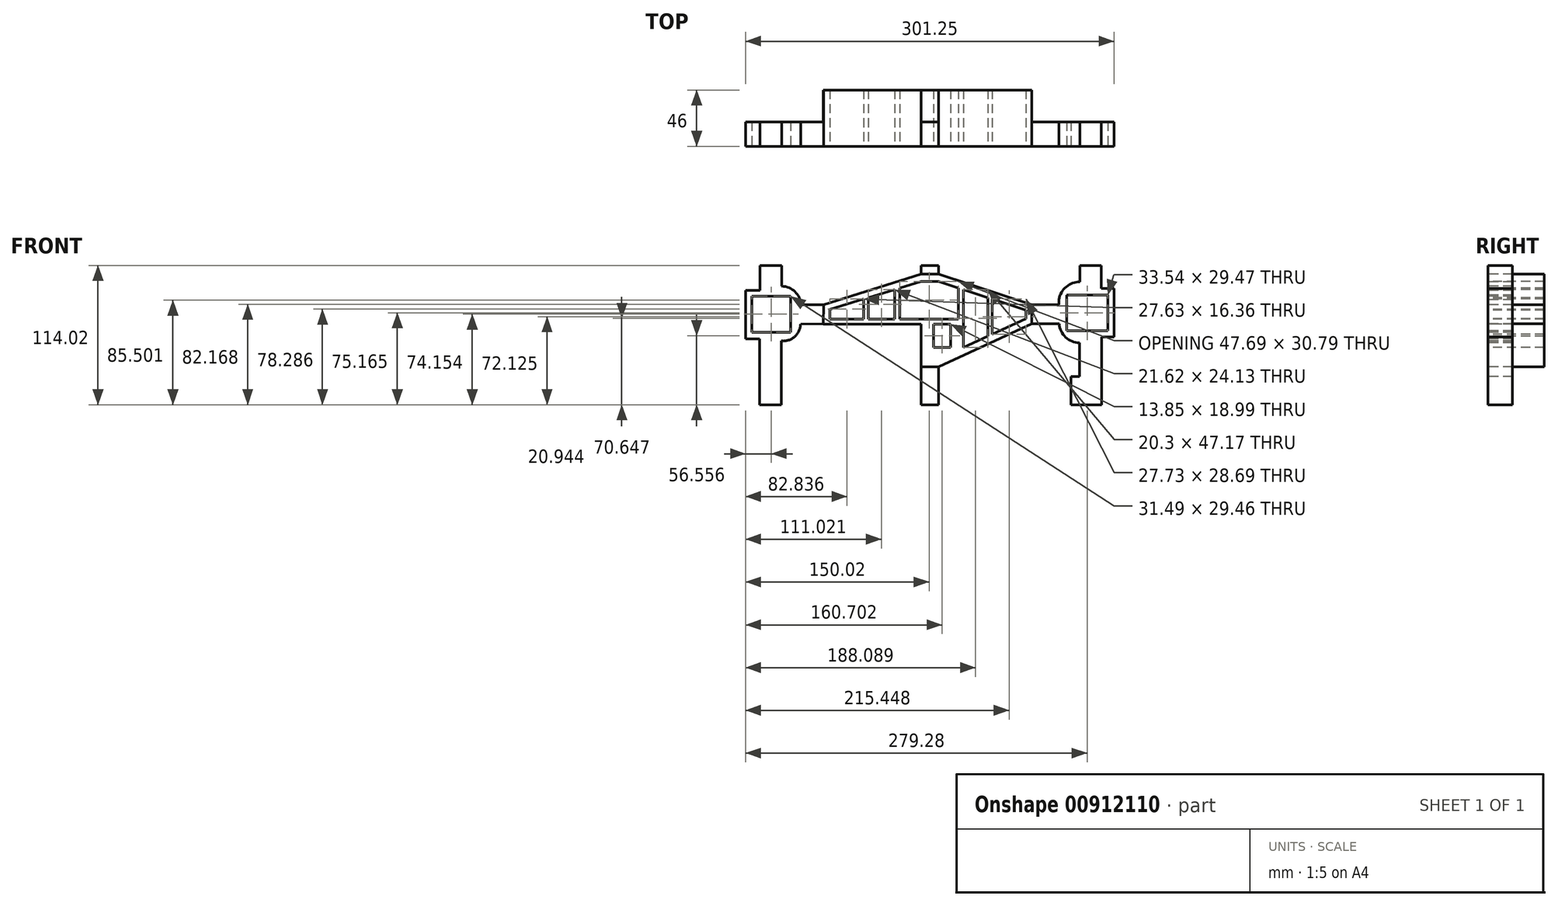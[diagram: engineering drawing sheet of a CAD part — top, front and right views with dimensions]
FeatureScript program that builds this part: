
annotation { "Feature Type Name" : "Feature", "Feature Type Description" : "" }
export const myFeature = defineFeature(function(context is Context, id is Id, definition is map)
    precondition{}
    {
        {
            var Q0;
            Q0=qCreatedBy(makeId("Front.planeOp"),FACE);
            var sketch = newSketch(context, id + "F0", { "sketchPlane" : qUnion([Q0])});
            skPoint(sketch, "E0.centerSnap0", {"position": v(-16.6, 78.73) * mm});
            skPoint(sketch, "E1.end.orphan", {"position": v(95.9, 7.77) * mm});
            skPoint(sketch, "E2.trimOffspring.end.orphan", {"position": v(-16.6, -51.27) * mm});
            skPoint(sketch, "E3.trimOffspring.end.orphan", {"position": v(97, 81.09) * mm});
            skPoint(sketch, "E4.endSnap0", {"position": v(95.9, 12.77) * mm});
            skPoint(sketch, "E5.trimOffspring.end.orphan", {"position": v(95.9, 11.34) * mm});
            skLineSegment(sketch, "E6.trimOffspring", {"start": v(-141.6, 27.34) * mm, "end": v(-141.6, 27.21) * mm});
            skLineSegment(sketch, "E7", {"start": v(-155.63, 47.28) * mm, "end": v(-155.63, 67.63) * mm});
            skLineSegment(sketch, "E8", {"start": v(-137.79, 50.54) * mm, "end": v(-137.79, 67.63) * mm});
            skArc(sketch, "E9", {"start": v(-122.48, 35.44) * mm, "mid": v(-127.04, 46.13) * mm, "end": v(-137.79, 50.54) * mm});
            skLineSegment(sketch, "E10", {"start": v(-155.63, 47.28) * mm, "end": v(-167.43, 47.28) * mm});
            skLineSegment(sketch, "E11", {"start": v(-155.87, 7.65) * mm, "end": v(-167.43, 7.65) * mm});
            skArc(sketch, "E12", {"start": v(88.97, 19.87) * mm, "mid": v(94.32, 8.84) * mm, "end": v(105.67, 4.2) * mm});
            skArc(sketch, "E13", {"start": v(106.05, 54.28) * mm, "mid": v(94.73, 50.14) * mm, "end": v(88.74, 39.68) * mm});
            skLineSegment(sketch, "E14", {"start": v(123.75, 9.23) * mm, "end": v(133.82, 9.23) * mm});
            skLineSegment(sketch, "E15", {"start": v(123.42, 67.63) * mm, "end": v(123.42, 48.8) * mm});
            skLineSegment(sketch, "E16", {"start": v(106.05, 54.28) * mm, "end": v(106.05, 67.63) * mm});
            skLineSegment(sketch, "E17", {"start": v(105.67, 4.2) * mm, "end": v(105.67, -23.42) * mm});
            skLineSegment(sketch, "E18", {"start": v(123.75, 9.23) * mm, "end": v(123.75, -42.87) * mm});
            skLineSegment(sketch, "E19", {"start": v(-122.48, 35.44) * mm, "end": v(-103.75, 35.44) * mm});
            skLineSegment(sketch, "E20", {"start": v(-122.48, 19.66) * mm, "end": v(-103.97, 19.73) * mm});
            skLineSegment(sketch, "E21", {"start": v(-103.75, 35.44) * mm, "end": v(-23.98, 60.68) * mm});
            skLineSegment(sketch, "E22", {"start": v(-23.98, -15.49) * mm, "end": v(-23.98, -46.39) * mm});
            skLineSegment(sketch, "E23", {"start": v(-9.79, -15.49) * mm, "end": v(-9.79, -46.39) * mm});
            skLineSegment(sketch, "E24", {"start": v(-23.98, 60.68) * mm, "end": v(-23.98, 67.63) * mm});
            skLineSegment(sketch, "E25", {"start": v(-9.79, 60.57) * mm, "end": v(-9.79, 67.63) * mm});
            skLineSegment(sketch, "E26", {"start": v(-103.97, 19.73) * mm, "end": v(-103.8, 19.66) * mm});
            skLineSegment(sketch, "E27", {"start": v(-9.79, -15.49) * mm, "end": v(66.68, 19.87) * mm});
            skLineSegment(sketch, "E28", {"start": v(-23.98, 54.5) * mm, "end": v(-9.79, 54.5) * mm});
            skLineSegment(sketch, "E29", {"start": v(88.74, 35.45) * mm, "end": v(88.74, 39.68) * mm});
            skLineSegment(sketch, "E30.trimOffspring", {"start": v(66.68, 35.45) * mm, "end": v(88.74, 35.45) * mm});
            skPoint(sketch, "E31.end.orphan", {"position": v(-103.75, 29.5) * mm});
            skPoint(sketch, "E32.orphan", {"position": v(-103.75, 25.95) * mm});
            skLineSegment(sketch, "E33", {"start": v(-98.4, 23.71) * mm, "end": v(-98.4, 31.56) * mm});
            skLineSegment(sketch, "E34", {"start": v(-98.4, 31.56) * mm, "end": v(-70.78, 40.08) * mm});
            skLineSegment(sketch, "E35", {"start": v(-9.79, 60.57) * mm, "end": v(66.68, 35.45) * mm});
            skLineSegment(sketch, "E36", {"start": v(-9.79, 54.5) * mm, "end": v(6.43, 49.18) * mm});
            skLineSegment(sketch, "E37", {"start": v(61.88, 30.97) * mm, "end": v(61.88, 23.97) * mm});
            skLineSegment(sketch, "E38", {"start": v(61.88, 23.97) * mm, "end": v(34.15, 11.4) * mm});
            skLineSegment(sketch, "E39.trimOffspring", {"start": v(66.68, 19.87) * mm, "end": v(88.97, 19.87) * mm});
            skLineSegment(sketch, "E40", {"start": v(98.61, -25.17) * mm, "end": v(98.61, -46.39) * mm});
            skLineSegment(sketch, "E41", {"start": v(-70.78, 40.08) * mm, "end": v(-70.78, 23.71) * mm});
            skLineSegment(sketch, "E42", {"start": v(-67.22, 41.18) * mm, "end": v(-67.22, 23.71) * mm});
            skLineSegment(sketch, "E43.trimOffspring", {"start": v(-67.22, 41.18) * mm, "end": v(-45.6, 47.84) * mm});
            skLineSegment(sketch, "E44.trimOffspring", {"start": v(-89.2, 19.66) * mm, "end": v(-89.63, 19.85) * mm});
            skLineSegment(sketch, "E45", {"start": v(98.61, -25.17) * mm, "end": v(98.61, -23.42) * mm});
            skLineSegment(sketch, "E46", {"start": v(98.61, -23.42) * mm, "end": v(105.67, -23.42) * mm});
            skLineSegment(sketch, "E47", {"start": v(34.15, 40.08) * mm, "end": v(34.15, 11.4) * mm});
            skLineSegment(sketch, "E48", {"start": v(30.8, 41.18) * mm, "end": v(30.8, 9.88) * mm});
            skLineSegment(sketch, "E49.trimOffspring", {"start": v(34.15, 40.08) * mm, "end": v(61.88, 30.97) * mm});
            skLineSegment(sketch, "E50.trimOffspring", {"start": v(30.8, 9.88) * mm, "end": v(10.51, 0.67) * mm});
            skLineSegment(sketch, "E51", {"start": v(-45.6, 47.84) * mm, "end": v(-45.6, 23.71) * mm});
            skLineSegment(sketch, "E52", {"start": v(-41.26, 49.18) * mm, "end": v(-41.26, 23.71) * mm});
            skLineSegment(sketch, "E53", {"start": v(6.43, 49.18) * mm, "end": v(6.43, 23.71) * mm});
            skLineSegment(sketch, "E54", {"start": v(10.51, 47.84) * mm, "end": v(10.51, 0.67) * mm});
            skLineSegment(sketch, "E55.trimOffspring", {"start": v(-41.26, 49.18) * mm, "end": v(-23.98, 54.5) * mm});
            skLineSegment(sketch, "E56.trimOffspring", {"start": v(10.51, 47.84) * mm, "end": v(30.8, 41.18) * mm});
            skLineSegment(sketch, "E57.trimOffspring", {"start": v(-103.8, 35.44) * mm, "end": v(-103.8, 19.66) * mm});
            skLineSegment(sketch, "E58.trimOffspring", {"start": v(66.68, 19.87) * mm, "end": v(66.68, 35.45) * mm});
            skLineSegment(sketch, "E59", {"start": v(-103.8, 19.66) * mm, "end": v(-23.98, 19.66) * mm});
            skLineSegment(sketch, "E60", {"start": v(-23.98, 19.66) * mm, "end": v(-23.98, -15.49) * mm});
            skLineSegment(sketch, "E61", {"start": v(-98.4, 23.71) * mm, "end": v(-70.78, 23.71) * mm});
            skLineSegment(sketch, "E62.bottom", {"start": v(-13.65, 19.66) * mm, "end": v(0.2, 19.66) * mm});
            skLineSegment(sketch, "E62.top", {"start": v(-13.65, 0.67) * mm, "end": v(0.2, 0.67) * mm});
            skLineSegment(sketch, "E62.left", {"start": v(-13.65, 19.66) * mm, "end": v(-13.65, 0.67) * mm});
            skLineSegment(sketch, "E62.right", {"start": v(0.2, 19.66) * mm, "end": v(0.2, 0.67) * mm});
            skLineSegment(sketch, "E63.trimOffspring", {"start": v(-67.22, 23.71) * mm, "end": v(-45.6, 23.71) * mm});
            skLineSegment(sketch, "E64.trimOffspring", {"start": v(-41.26, 23.71) * mm, "end": v(6.43, 23.71) * mm});
            skLineSegment(sketch, "E65", {"start": v(-23.98, 60.68) * mm, "end": v(-9.79, 60.57) * mm});
            skPoint(sketch, "E66.start.orphan", {"position": v(-103.75, 77.48) * mm});
            skPoint(sketch, "E67.start.orphan", {"position": v(66.68, -52.27) * mm});
            skLineSegment(sketch, "E68", {"start": v(-23.98, -15.49) * mm, "end": v(-9.79, -15.49) * mm});
            skLineSegment(sketch, "E69", {"start": v(123.42, 48.8) * mm, "end": v(133.82, 48.8) * mm});
            skLineSegment(sketch, "E70", {"start": v(-155.63, 67.63) * mm, "end": v(-137.79, 67.63) * mm});
            skLineSegment(sketch, "E71", {"start": v(-167.43, 47.28) * mm, "end": v(-167.43, 7.65) * mm});
            skLineSegment(sketch, "E72", {"start": v(-138.17, -46.38) * mm, "end": v(-155.87, -46.36) * mm});
            skLineSegment(sketch, "E73", {"start": v(-138.17, 5.8) * mm, "end": v(-138.17, -46.38) * mm});
            skLineSegment(sketch, "E74", {"start": v(-155.87, 7.65) * mm, "end": v(-155.87, -46.36) * mm});
            skLineSegment(sketch, "E75", {"start": v(-23.98, -46.39) * mm, "end": v(-9.79, -46.39) * mm});
            skLineSegment(sketch, "E76", {"start": v(98.61, -46.39) * mm, "end": v(123.75, -46.39) * mm});
            skPoint(sketch, "E77.orphan", {"position": v(-167.43, -46.35) * mm});
            skPoint(sketch, "E78.start.orphan", {"position": v(-174.59, -41.81) * mm});
            skPoint(sketch, "E79.start.orphan", {"position": v(-164.6, -52.27) * mm});
            skLineSegment(sketch, "E80", {"start": v(106.05, 67.63) * mm, "end": v(123.42, 67.63) * mm});
            skLineSegment(sketch, "E81", {"start": v(133.82, 48.8) * mm, "end": v(133.82, 9.23) * mm});
            skLineSegment(sketch, "E82", {"start": v(123.75, -42.87) * mm, "end": v(123.75, -46.39) * mm});
            skPoint(sketch, "E83.center.orphan", {"position": v(132.35, -42.27) * mm});
            skPoint(sketch, "E83.end.orphan", {"position": v(142.34, -42.53) * mm});
            skPoint(sketch, "E84.orphan", {"position": v(133.82, -46.39) * mm});
            skPoint(sketch, "E85.end.orphan", {"position": v(132.35, 77.22) * mm});
            skPoint(sketch, "E85.start.orphan", {"position": v(142.34, 68.42) * mm});
            skLineSegment(sketch, "E86", {"start": v(-23.98, 67.63) * mm, "end": v(-9.79, 67.63) * mm});
            skPoint(sketch, "E87.orphan", {"position": v(-122.48, -46.4) * mm});
            skPoint(sketch, "E88.start.orphan", {"position": v(-158.57, 67.63) * mm});
            skPoint(sketch, "E89.center.orphan", {"position": v(-164.6, 67.54) * mm});
            skPoint(sketch, "E89.end.orphan", {"position": v(-174.59, 67.83) * mm});
            skPoint(sketch, "E90", {"position": v(-45.6, 53.83) * mm});
            skPoint(sketch, "E91", {"position": v(10.51, 53.9) * mm});
            skPoint(sketch, "E92.firstSnap0", {"position": v(128.62, 48.8) * mm});
            skLineSegment(sketch, "E92.bottom", {"start": v(128.62, 43.51) * mm, "end": v(95.08, 43.51) * mm});
            skLineSegment(sketch, "E92.top", {"start": v(128.62, 14.04) * mm, "end": v(95.08, 14.04) * mm});
            skLineSegment(sketch, "E92.left", {"start": v(128.62, 43.51) * mm, "end": v(128.62, 14.04) * mm});
            skLineSegment(sketch, "E92.right", {"start": v(95.08, 43.51) * mm, "end": v(95.08, 14.04) * mm});
            skLineSegment(sketch, "E93.bottom", {"start": v(-130.74, 42.5) * mm, "end": v(-162.23, 42.5) * mm});
            skLineSegment(sketch, "E93.top", {"start": v(-130.74, 13.03) * mm, "end": v(-162.23, 13.03) * mm});
            skLineSegment(sketch, "E93.left", {"start": v(-130.74, 42.5) * mm, "end": v(-130.74, 13.03) * mm});
            skLineSegment(sketch, "E93.right", {"start": v(-162.23, 42.5) * mm, "end": v(-162.23, 13.03) * mm});
            skLineSegment(sketch, "E94", {"start": v(123.42, 67.63) * mm, "end": v(106.05, 67.63) * mm});
            skLineSegment(sketch, "E95", {"start": v(-155.87, -46.36) * mm, "end": v(-138.17, -46.36) * mm});
            skArc(sketch, "E96", {"start": v(-138.17, 5.8) * mm, "mid": v(-127.34, 9.35) * mm, "end": v(-122.48, 19.66) * mm});
            skLineSegment(sketch, "E97.bottom", {"start": v(-162.23, 42.5) * mm, "end": v(-154.97, 42.5) * mm});
            skLineSegment(sketch, "E97.left", {"start": v(-162.23, 42.5) * mm, "end": v(-162.23, 35.57) * mm});
            skLineSegment(sketch, "E98.trimOffspring", {"start": v(-137.79, 67.63) * mm, "end": v(-155.63, 67.63) * mm});
            skLineSegment(sketch, "E99.trimOffspring", {"start": v(-9.79, 67.63) * mm, "end": v(-23.98, 67.63) * mm});
            skLineSegment(sketch, "E100.trimOffspring", {"start": v(-23.98, -46.37) * mm, "end": v(-9.79, -46.37) * mm});
            skSolve(sketch);
        }
        {
            var Q0;
            Q0=makeQuery(id+"F0.imprint","IMPRINT",FACE,{"disambiguationData":[TD([[makeQuery(id+"F0.imprint","IMPRINT",EDGE,{"derivedFrom":sQuery(id+"F0.wireOp",EDGE,"E7")}),-1.0]])]});
            var Q1;
            Q1=makeQuery(id+"F0.imprint","IMPRINT",FACE,{"disambiguationData":[TD([[makeQuery(id+"F0.imprint","IMPRINT",EDGE,{"derivedFrom":sQuery(id+"F0.wireOp",EDGE,"aa85290f-87d0-496b-9952-a54aab5139fa")}),-1.0]])]});
            var Q2;
            Q2=makeQuery(id+"F0.imprint","IMPRINT",FACE,{"disambiguationData":[TD([[makeQuery(id+"F0.imprint","IMPRINT",EDGE,{"derivedFrom":sQuery(id+"F0.wireOp",EDGE,"E22")}),1.0]])]});
            var Q3;
            Q3=makeQuery(id+"F0.imprint","IMPRINT",FACE,{"disambiguationData":[TD([[makeQuery(id+"F0.imprint","IMPRINT",EDGE,{"derivedFrom":sQuery(id+"F0.wireOp",EDGE,"E24")}),-1.0]])]});
            var Q4;
            Q4=makeQuery(id+"F0.imprint","IMPRINT",FACE,{"disambiguationData":[TD([[makeQuery(id+"F0.imprint","IMPRINT",EDGE,{"derivedFrom":sQuery(id+"F0.wireOp",EDGE,"E13")}),1.0]])]});
            extrude(context, id + "F1", {"entities" : qUnion([Q0, Q1, Q2, Q3, Q4]), "oppositeDirection" : true, "depth" : 20 * mm, "offsetDistance" : 25 * mm});
        }
        {
            var Q0;
            {var subQ0=sQuery(id+"F0.wireOp",EDGE,"E21");Q0=makeQuery(id+"F0.imprint","IMPRINT",FACE,{"disambiguationData":[TD([[makeQuery(id+"F0.imprint","IMPRINT",EDGE,{"derivedFrom":subQ0}),-1.0]])]});}
            extrude(context, id + "F2", {"entities" : qUnion([Q0]), "oppositeDirection" : true, "depth" : 46 * mm, "offsetDistance" : 25 * mm});
        }
    });
